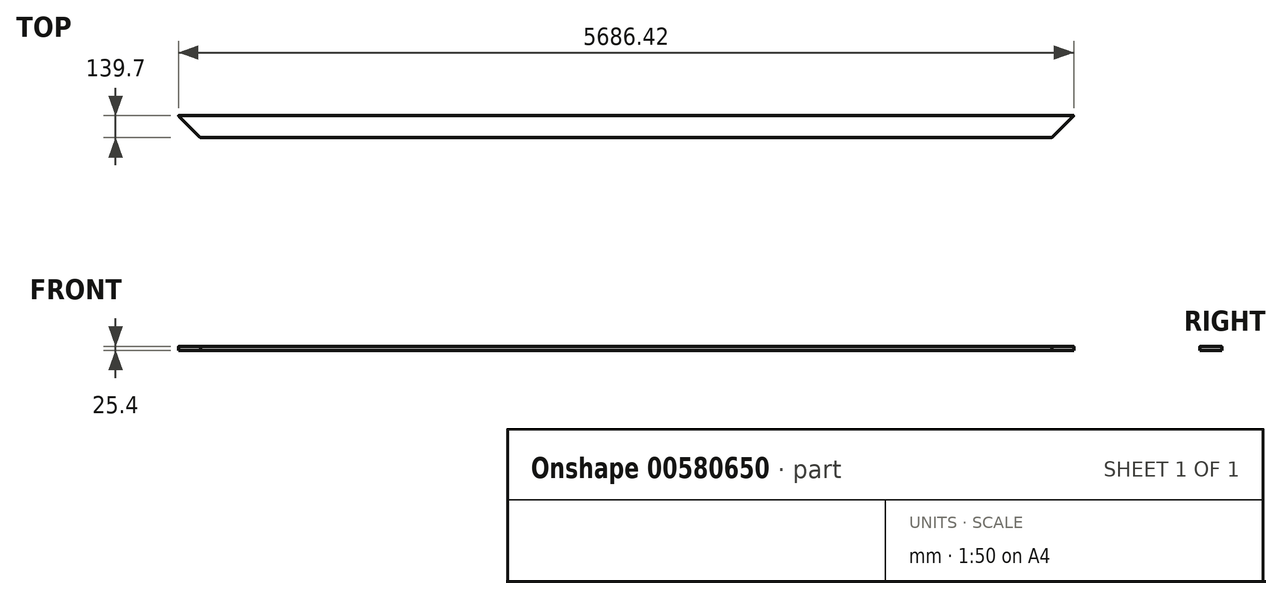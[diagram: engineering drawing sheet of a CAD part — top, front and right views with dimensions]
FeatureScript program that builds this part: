
annotation { "Feature Type Name" : "Feature", "Feature Type Description" : "" }
export const myFeature = defineFeature(function(context is Context, id is Id, definition is map)
    precondition{}
    {
        {
            var Q0;
            Q0=qCreatedBy(makeId("Top.planeOp"),FACE);
            var sketch = newSketch(context, id + "F0", { "sketchPlane" : qUnion([Q0])});
            skLineSegment(sketch, "E0.bottom", {"start": v(2775.66, -1496.74) * mm, "end": v(-2631.36, -1496.74) * mm});
            skLineSegment(sketch, "E0.top", {"start": v(2915.36, -1357.04) * mm, "end": v(-2771.06, -1357.04) * mm});
            skPoint(sketch, "E0.middle", {"position": v(0, 0) * mm});
            skLineSegment(sketch, "E1", {"start": v(2915.36, -1357.04) * mm, "end": v(2775.66, -1496.74) * mm});
            skLineSegment(sketch, "E2", {"start": v(-2771.06, -1357.04) * mm, "end": v(-2631.36, -1496.74) * mm});
            skSolve(sketch);
        }
        {
            var Q0;
            Q0=makeQuery(id+"F0.imprint","IMPRINT",FACE,{"disambiguationData":[TD([[makeQuery(id+"F0.imprint","IMPRINT",EDGE,{"derivedFrom":sQuery(id+"F0.wireOp",EDGE,"E0.bottom")}),-1.0]])]});
            extrude(context, id + "F1", {"entities" : qUnion([Q0]), "depth" : 25.4 * mm, "offsetDistance" : 25.4 * mm});
        }
        {
            var Q0;
            Q0=makeQuery(id+"F1.opExtrude","CAP_EDGE",EDGE,{"disambiguationData":[OSD([sQuery(id+"F0.wireOp",EDGE,"E0.top")])],"isStart":false});
            var Q1;
            Q1=makeQuery(id+"F1.opExtrude","CAP_EDGE",EDGE,{"disambiguationData":[OSD([sQuery(id+"F0.wireOp",EDGE,"E0.bottom")])],"isStart":false});
            fillet(context, id + "F2", {"entities" : qUnion([Q0, Q1]), "radius" : 5.08 * mm, "tangentPropagation" : true, "allowEdgeOverflow" : false});
        }
    });
